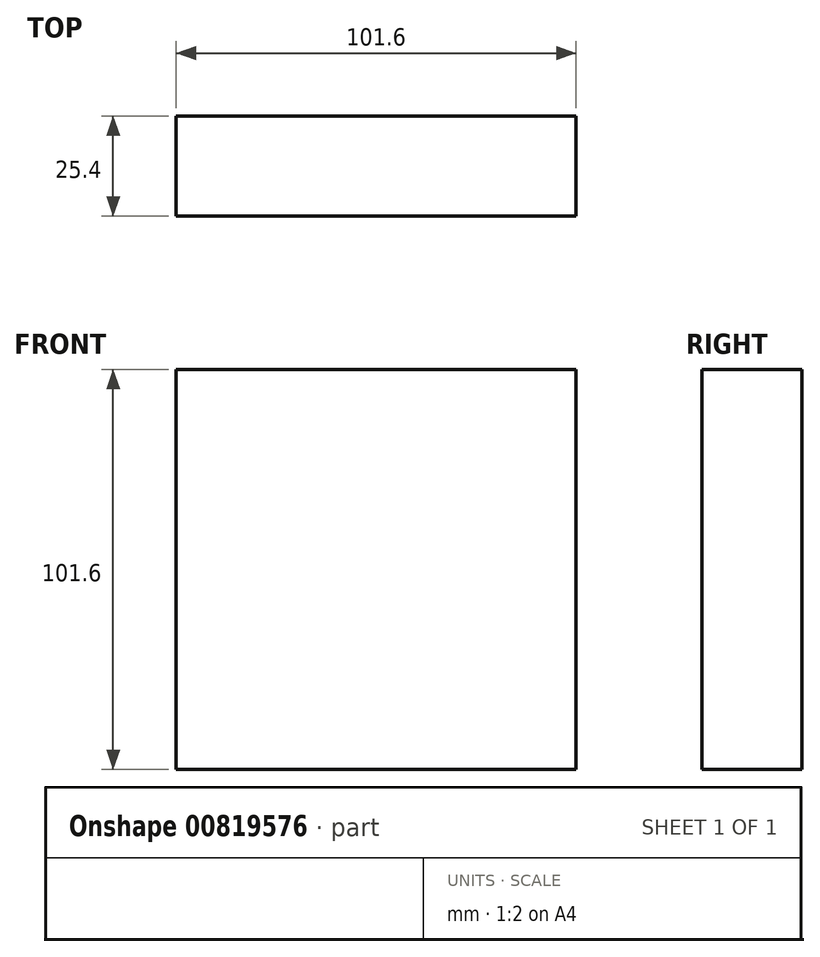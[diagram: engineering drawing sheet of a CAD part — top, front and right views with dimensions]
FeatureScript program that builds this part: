
annotation { "Feature Type Name" : "Feature", "Feature Type Description" : "" }
export const myFeature = defineFeature(function(context is Context, id is Id, definition is map)
    precondition{}
    {
        {
            var Q0;
            Q0=qCreatedBy(makeId("Front.planeOp"),FACE);
            var sketch = newSketch(context, id + "F0", { "sketchPlane" : qUnion([Q0])});
            skLineSegment(sketch, "E0.bottom", {"start": v(-50.8, 50.8) * mm, "end": v(50.8, 50.8) * mm});
            skLineSegment(sketch, "E0.top", {"start": v(-50.8, -50.8) * mm, "end": v(50.8, -50.8) * mm});
            skLineSegment(sketch, "E0.left", {"start": v(-50.8, 50.8) * mm, "end": v(-50.8, -50.8) * mm});
            skLineSegment(sketch, "E0.right", {"start": v(50.8, 50.8) * mm, "end": v(50.8, -50.8) * mm});
            skPoint(sketch, "E0.middle", {"position": v(0, 0) * mm});
            skSolve(sketch);
        }
        {
            var Q0;
            Q0 = qSketchRegion(id + "F0", true);
            extrude(context, id + "F1", {"entities" : qUnion([Q0]), "depth" : 25.4 * mm, "offsetDistance" : 25.4 * mm});
        }
    });
